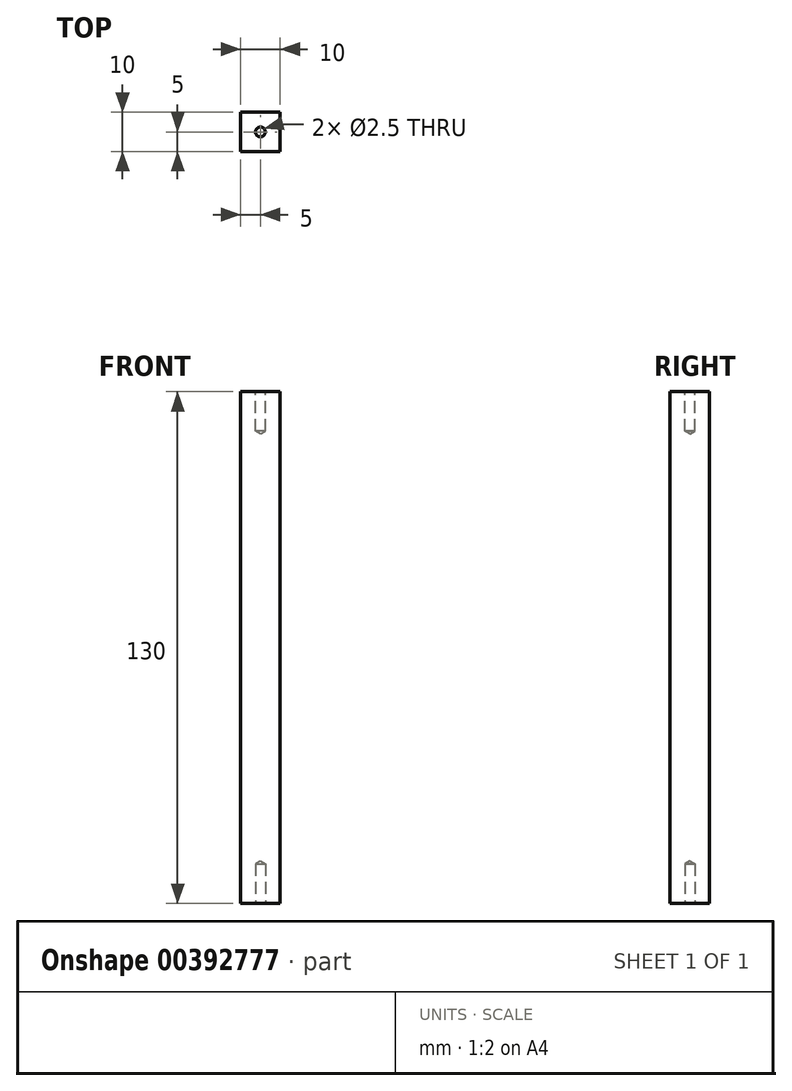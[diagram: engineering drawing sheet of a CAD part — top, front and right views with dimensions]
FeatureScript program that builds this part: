
annotation { "Feature Type Name" : "Feature", "Feature Type Description" : "" }
export const myFeature = defineFeature(function(context is Context, id is Id, definition is map)
    precondition{}
    {
        {
            var Q0;
            Q0=qCreatedBy(makeId("Top.planeOp"),FACE);
            var sketch = newSketch(context, id + "F0", { "sketchPlane" : qUnion([Q0])});
            skLineSegment(sketch, "E0.bottom", {"start": v(0, 0) * mm, "end": v(10, 0) * mm});
            skLineSegment(sketch, "E0.top", {"start": v(0, 10) * mm, "end": v(10, 10) * mm});
            skLineSegment(sketch, "E0.left", {"start": v(0, 0) * mm, "end": v(0, 10) * mm});
            skLineSegment(sketch, "E0.right", {"start": v(10, 0) * mm, "end": v(10, 10) * mm});
            skSolve(sketch);
        }
        {
            var Q0;
            Q0 = qSketchRegion(id + "F0", true);
            extrude(context, id + "F1", {"entities" : qUnion([Q0]), "depth" : 130 * mm});
        }
        {
            var Q0;
            Q0=makeQuery(id+"F1.opExtrude","CAP_FACE",FACE,{"disambiguationData":[OSD([sQuery(id+"F0.wireOp",EDGE,"E0.bottom"),sQuery(id+"F0.wireOp",EDGE,"E0.top"),sQuery(id+"F0.wireOp",EDGE,"E0.left"),sQuery(id+"F0.wireOp",EDGE,"E0.right")])],"isStart":true});
            var sketch = newSketch(context, id + "F2", { "sketchPlane" : qUnion([Q0])});
            skLineSegment(sketch, "E1.bottom", {"start": v(0, 0) * mm, "end": v(5, 0) * mm});
            skLineSegment(sketch, "E1.top", {"start": v(0, -5) * mm, "end": v(5, -5) * mm});
            skLineSegment(sketch, "E1.left", {"start": v(0, 0) * mm, "end": v(0, -5) * mm});
            skLineSegment(sketch, "E1.right", {"start": v(5, 0) * mm, "end": v(5, -5) * mm});
            skSolve(sketch);
        }
        {
            var Q0;
            Q0=sQuery(id+"F2.wireOp",VERTEX,"E1.top.end");
            var Q1;
            Q1=makeQuery(id+"F1.opExtrude","SWEPT_BODY",BODY,{"disambiguationData":[OSD([sQuery(id+"F0.wireOp",EDGE,"E0.bottom"),sQuery(id+"F0.wireOp",EDGE,"E0.top"),sQuery(id+"F0.wireOp",EDGE,"E0.left"),sQuery(id+"F0.wireOp",EDGE,"E0.right")])]});
            hole(context, id + "F3", {"style" : HoleStyle.SIMPLE, "endStyle" : HoleEndStyle.BLIND, "holeDiameter" : 2.5 * mm, "holeDepth" : 10 * mm, "isTappedThrough" : true, "tappedDepth" : 12 * mm, "tapClearance" : 3, "locations" : qUnion([Q0]), "scope" : qUnion([Q1])});
        }
        {
            var Q0;
            Q0=makeQuery(id+"F1.opExtrude","CAP_FACE",FACE,{"disambiguationData":[OSD([sQuery(id+"F0.wireOp",EDGE,"E0.bottom"),sQuery(id+"F0.wireOp",EDGE,"E0.top"),sQuery(id+"F0.wireOp",EDGE,"E0.left"),sQuery(id+"F0.wireOp",EDGE,"E0.right")])],"isStart":false});
            var sketch = newSketch(context, id + "F4", { "sketchPlane" : qUnion([Q0])});
            skLineSegment(sketch, "E2.bottom", {"start": v(0, 0) * mm, "end": v(5, 0) * mm});
            skLineSegment(sketch, "E2.top", {"start": v(0, 5) * mm, "end": v(5, 5) * mm});
            skLineSegment(sketch, "E2.left", {"start": v(0, 0) * mm, "end": v(0, 5) * mm});
            skLineSegment(sketch, "E2.right", {"start": v(5, 0) * mm, "end": v(5, 5) * mm});
            skSolve(sketch);
        }
        {
            var Q0;
            Q0=sQuery(id+"F4.wireOp",VERTEX,"E2.right.end");
            var Q1;
            Q1=makeQuery(id+"F1.opExtrude","SWEPT_BODY",BODY,{"disambiguationData":[OSD([sQuery(id+"F0.wireOp",EDGE,"E0.bottom"),sQuery(id+"F0.wireOp",EDGE,"E0.top"),sQuery(id+"F0.wireOp",EDGE,"E0.left"),sQuery(id+"F0.wireOp",EDGE,"E0.right")])]});
            hole(context, id + "F5", {"style" : HoleStyle.SIMPLE, "endStyle" : HoleEndStyle.BLIND, "holeDiameter" : 2.5 * mm, "holeDepth" : 10 * mm, "isTappedThrough" : true, "tappedDepth" : 12 * mm, "tapClearance" : 3, "locations" : qUnion([Q0]), "scope" : qUnion([Q1])});
        }
    });
